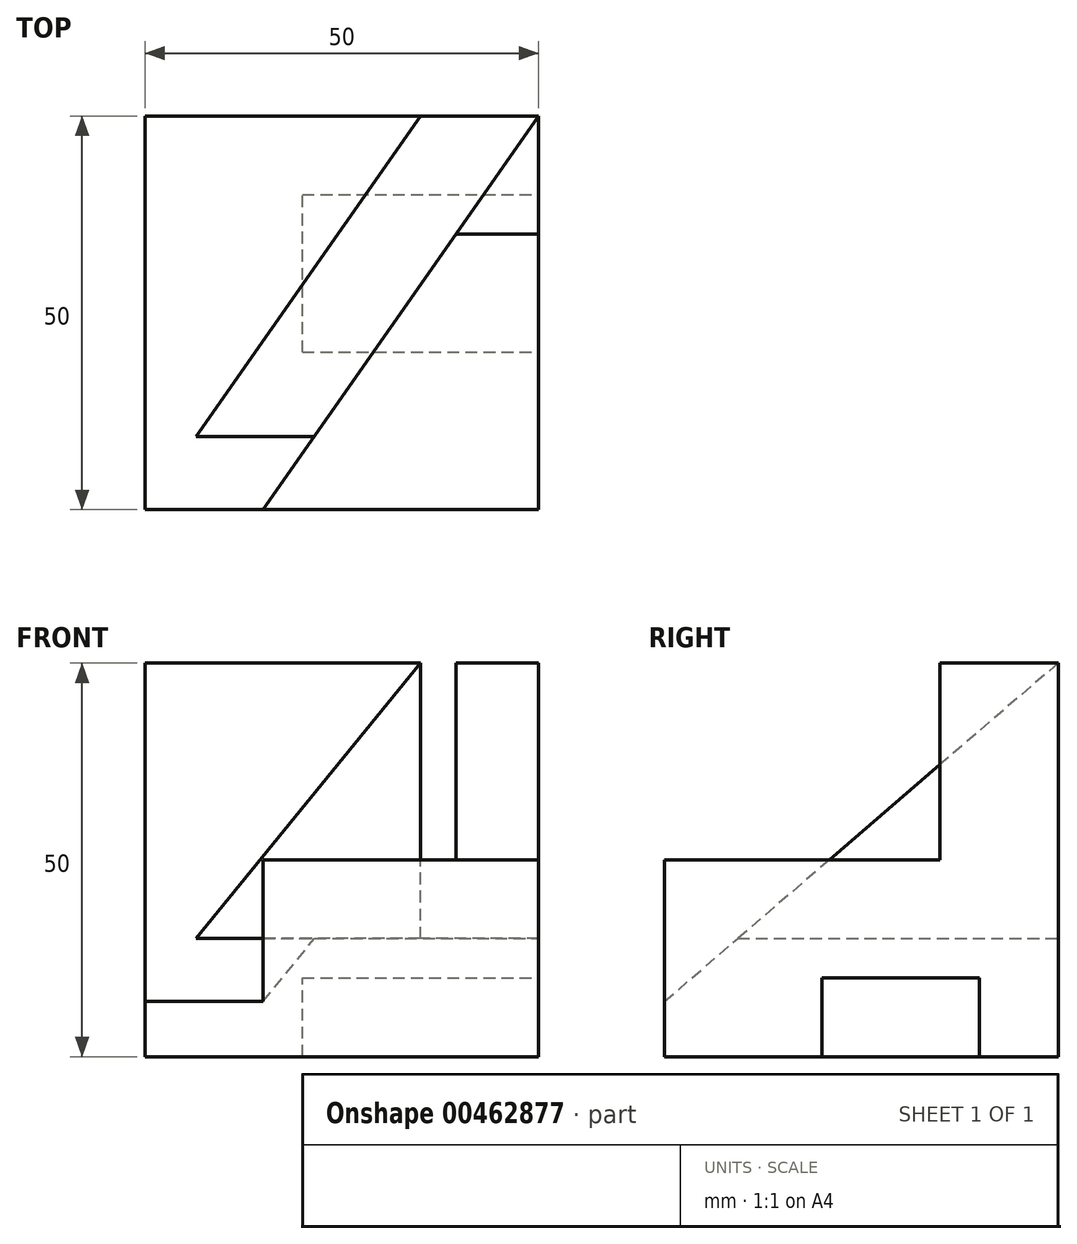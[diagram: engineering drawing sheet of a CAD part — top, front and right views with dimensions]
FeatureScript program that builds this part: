
annotation { "Feature Type Name" : "Feature", "Feature Type Description" : "" }
export const myFeature = defineFeature(function(context is Context, id is Id, definition is map)
    precondition{}
    {
        {
            var Q0;
            Q0=qCreatedBy(makeId("Front.planeOp"),FACE);
            var sketch = newSketch(context, id + "F0", { "sketchPlane" : qUnion([Q0])});
            skLineSegment(sketch, "E0.bottom", {"start": v(0, 0) * mm, "end": v(50, 0) * mm});
            skLineSegment(sketch, "E0.top", {"start": v(0, 50) * mm, "end": v(50, 50) * mm});
            skLineSegment(sketch, "E0.left", {"start": v(0, 0) * mm, "end": v(0, 50) * mm});
            skLineSegment(sketch, "E0.right", {"start": v(50, 0) * mm, "end": v(50, 50) * mm});
            skSolve(sketch);
        }
        {
            var Q0;
            Q0=makeQuery(id+"F0.imprint","IMPRINT",FACE,{"disambiguationData":[TD([[makeQuery(id+"F0.imprint","IMPRINT",EDGE,{"derivedFrom":sQuery(id+"F0.wireOp",EDGE,"E0.bottom")}),1.0]])]});
            extrude(context, id + "F1", {"entities" : qUnion([Q0]), "depth" : 50 * mm});
        }
        {
            var Q0;
            Q0=makeQuery(id+"F1.opExtrude","SWEPT_FACE",FACE,{"disambiguationData":[OSD([sQuery(id+"F0.wireOp",EDGE,"E0.top")])]});
            var sketch = newSketch(context, id + "F2", { "sketchPlane" : qUnion([Q0])});
            skLineSegment(sketch, "E1", {"start": v(50, 0) * mm, "end": v(35, 0) * mm});
            skLineSegment(sketch, "E2", {"start": v(0, -50) * mm, "end": v(15, -50) * mm});
            skLineSegment(sketch, "E3", {"start": v(35, 0) * mm, "end": v(0, -50) * mm});
            skLineSegment(sketch, "E4", {"start": v(15, -50) * mm, "end": v(50, 0) * mm});
            skSolve(sketch);
        }
        {
            var Q0;
            Q0 = qSketchRegion(id + "F2", true);
            extrude(context, id + "F3", {"entities" : qUnion([Q0]), "operationType" : NewBodyOperationType.REMOVE, "oppositeDirection" : true, "depth" : 43 * mm});
        }
        {
            var Q0;
            {var subQ0=sQuery(id+"F0.wireOp",EDGE,"E0.right");var subQ1=sQuery(id+"F0.wireOp",EDGE,"E0.top");Q0=makeQuery(id+"F3.boolean.opBoolean","SPLIT",FACE,{"disambiguationData":[TD([makeQuery(id+"F1.opExtrude","SWEPT_FACE",FACE,{"disambiguationData":[OSD([subQ0])]})])],"derivedFrom":makeQuery(id+"F1.opExtrude","SWEPT_FACE",FACE,{"disambiguationData":[OSD([subQ1])]})});}
            var sketch = newSketch(context, id + "F4", { "sketchPlane" : qUnion([Q0])});
            skLineSegment(sketch, "E5", {"start": v(50, 0) * mm, "end": v(50, -15) * mm});
            skLineSegment(sketch, "E6", {"start": v(50, -15) * mm, "end": v(39.5, -15) * mm});
            skSolve(sketch);
        }
        {
            var Q0;
            {var subQ0=sQuery(id+"F4.wireOp",EDGE,"E6");Q0=makeQuery(id+"F4.imprint","IMPRINT",FACE,{"disambiguationData":[TD([[makeQuery(id+"F4.imprint","IMPRINT",EDGE,{"derivedFrom":subQ0}),1.0]])]});}
            extrude(context, id + "F5", {"entities" : qUnion([Q0]), "operationType" : NewBodyOperationType.REMOVE, "oppositeDirection" : true, "depth" : 25 * mm});
        }
        {
            var Q0;
            {var subQ0=sQuery(id+"F0.wireOp",EDGE,"E0.left");var subQ1=sQuery(id+"F0.wireOp",EDGE,"E0.top");Q0=makeQuery(id+"F3.boolean.opBoolean","SPLIT",FACE,{"disambiguationData":[TD([makeQuery(id+"F1.opExtrude","SWEPT_FACE",FACE,{"disambiguationData":[OSD([subQ0])]})])],"derivedFrom":makeQuery(id+"F1.opExtrude","SWEPT_FACE",FACE,{"disambiguationData":[OSD([subQ1])]})});}
            extrude(context, id + "F6", {"entities" : qUnion([Q0]), "operationType" : NewBodyOperationType.REMOVE, "oppositeDirection" : true, "depth" : 43 * mm});
        }
        {
            var Q0;
            Q0=makeQuery(id+"F1.opExtrude","SWEPT_FACE",FACE,{"disambiguationData":[OSD([sQuery(id+"F0.wireOp",EDGE,"E0.left")])]});
            var sketch = newSketch(context, id + "F7", { "sketchPlane" : qUnion([Q0])});
            skLineSegment(sketch, "E7", {"start": v(0, 50) * mm, "end": v(0, 7) * mm});
            skLineSegment(sketch, "E8", {"start": v(0, 7) * mm, "end": v(50, 7) * mm});
            skLineSegment(sketch, "E9", {"start": v(50, 7) * mm, "end": v(0, 50) * mm});
            skSolve(sketch);
        }
        {
            var Q0;
            Q0=makeQuery(id+"F7.imprint","IMPRINT",FACE,{"disambiguationData":[TD([[makeQuery(id+"F7.imprint","IMPRINT",EDGE,{"derivedFrom":sQuery(id+"F7.wireOp",EDGE,"E7")}),1.0]])]});
            var Q1;
            Q1=makeQuery(id+"F3.boolean.opBoolean","COPY",FACE,{"derivedFrom":makeQuery(id+"F3.opExtrude","SWEPT_FACE",FACE,{"disambiguationData":[OSD([sQuery(id+"F2.wireOp",EDGE,"E4")])]})});
            extrude(context, id + "F8", {"entities" : qUnion([Q0]), "operationType" : NewBodyOperationType.ADD, "endBound" : BoundingType.UP_TO_SURFACE, "oppositeDirection" : true, "endBoundEntityFace" : qUnion([Q1]), "depth" : 25 * mm});
        }
        {
            var Q0;
            Q0=qCreatedBy(makeId("Top.planeOp"),FACE);
            var Q1;
            {var subQ0=sQuery(id+"F2.wireOp",EDGE,"E4");var subQ1=sQuery(id+"F0.wireOp",EDGE,"E0.right");var subQ2=sQuery(id+"F0.wireOp",EDGE,"E0.top");Q1=makeQuery(id+"F8.boolean.opBoolean","MERGE",VERTEX,{"derivedFrom":[makeQuery(id+"F3.boolean.opBoolean","MERGE",VERTEX,{"derivedFrom":[makeQuery(id+"F1.opExtrude","CAP_VERTEX",VERTEX,{"disambiguationData":[OSD([subQ2,subQ1])],"isStart":true}),makeQuery(id+"F3.opExtrude","CAP_VERTEX",VERTEX,{"disambiguationData":[OSD([subQ2,subQ1,sQuery(id+"F2.wireOp",EDGE,"E1"),subQ0])],"isStart":true})]}),makeQuery(id+"F8.opExtrude","CAP_VERTEX",VERTEX,{"disambiguationData":[OSD([subQ0,sQuery(id+"F7.wireOp",EDGE,"E7"),sQuery(id+"F7.wireOp",EDGE,"E9")])],"isStart":false})]});}
            cPlane(context, id + "F9", {"entities" : qUnion([Q0, Q1]), "cplaneType" : CPlaneType.PLANE_POINT, "offset" : 25 * mm, "width" : 150 * mm, "height" : 150 * mm});
        }
        {
            var Q0;
            Q0=qCreatedBy(id+"F9.planeOp",FACE);
            var sketch = newSketch(context, id + "F10", { "sketchPlane" : qUnion([Q0])});
            skLineSegment(sketch, "E10", {"start": v(50, 0) * mm, "end": v(35, 0) * mm});
            skLineSegment(sketch, "E11", {"start": v(35, 0) * mm, "end": v(0, -50) * mm});
            skLineSegment(sketch, "E12", {"start": v(0, -50) * mm, "end": v(15, -50) * mm});
            skLineSegment(sketch, "E13", {"start": v(15, -50) * mm, "end": v(50, 0) * mm});
            skSolve(sketch);
        }
        {
            var Q0;
            Q0=makeQuery(id+"F1.opExtrude","SWEPT_FACE",FACE,{"disambiguationData":[OSD([sQuery(id+"F0.wireOp",EDGE,"E0.bottom")])]});
            cPlane(context, id + "F11", {"entities" : qUnion([Q0]), "cplaneType" : CPlaneType.OFFSET, "offset" : 15 * mm, "oppositeDirection" : true, "width" : 150 * mm, "height" : 150 * mm});
        }
        {
            var Q0;
            Q0=makeQuery(id+"F10.imprint","IMPRINT",FACE,{"disambiguationData":[TD([[makeQuery(id+"F10.imprint","IMPRINT",EDGE,{"derivedFrom":sQuery(id+"F10.wireOp",EDGE,"E10")}),1.0]])]});
            var Q1;
            Q1=qCreatedBy(id+"F11.planeOp",FACE);
            extrude(context, id + "F12", {"entities" : qUnion([Q0]), "operationType" : NewBodyOperationType.REMOVE, "endBound" : BoundingType.UP_TO_SURFACE, "oppositeDirection" : true, "endBoundEntityFace" : qUnion([Q1]), "depth" : 25 * mm});
        }
        {
            var Q0;
            Q0=makeQuery(id+"F1.opExtrude","SWEPT_FACE",FACE,{"disambiguationData":[OSD([sQuery(id+"F0.wireOp",EDGE,"E0.right")])]});
            var sketch = newSketch(context, id + "F13", { "sketchPlane" : qUnion([Q0])});
            skLineSegment(sketch, "E14", {"start": v(0, 0) * mm, "end": v(-10, 0) * mm});
            skLineSegment(sketch, "E15.bottom", {"start": v(-10, 0) * mm, "end": v(-30, 0) * mm});
            skLineSegment(sketch, "E15.top", {"start": v(-10, 10) * mm, "end": v(-30, 10) * mm});
            skLineSegment(sketch, "E15.left", {"start": v(-10, 0) * mm, "end": v(-10, 10) * mm});
            skLineSegment(sketch, "E15.right", {"start": v(-30, 0) * mm, "end": v(-30, 10) * mm});
            skSolve(sketch);
        }
        {
            var Q0;
            Q0=makeQuery(id+"F13.imprint","IMPRINT",FACE,{"disambiguationData":[TD([[makeQuery(id+"F13.imprint","IMPRINT",EDGE,{"derivedFrom":sQuery(id+"F13.wireOp",EDGE,"E15.bottom")}),1.0]])]});
            extrude(context, id + "F14", {"entities" : qUnion([Q0]), "operationType" : NewBodyOperationType.REMOVE, "oppositeDirection" : true, "depth" : 30 * mm});
        }
    });
